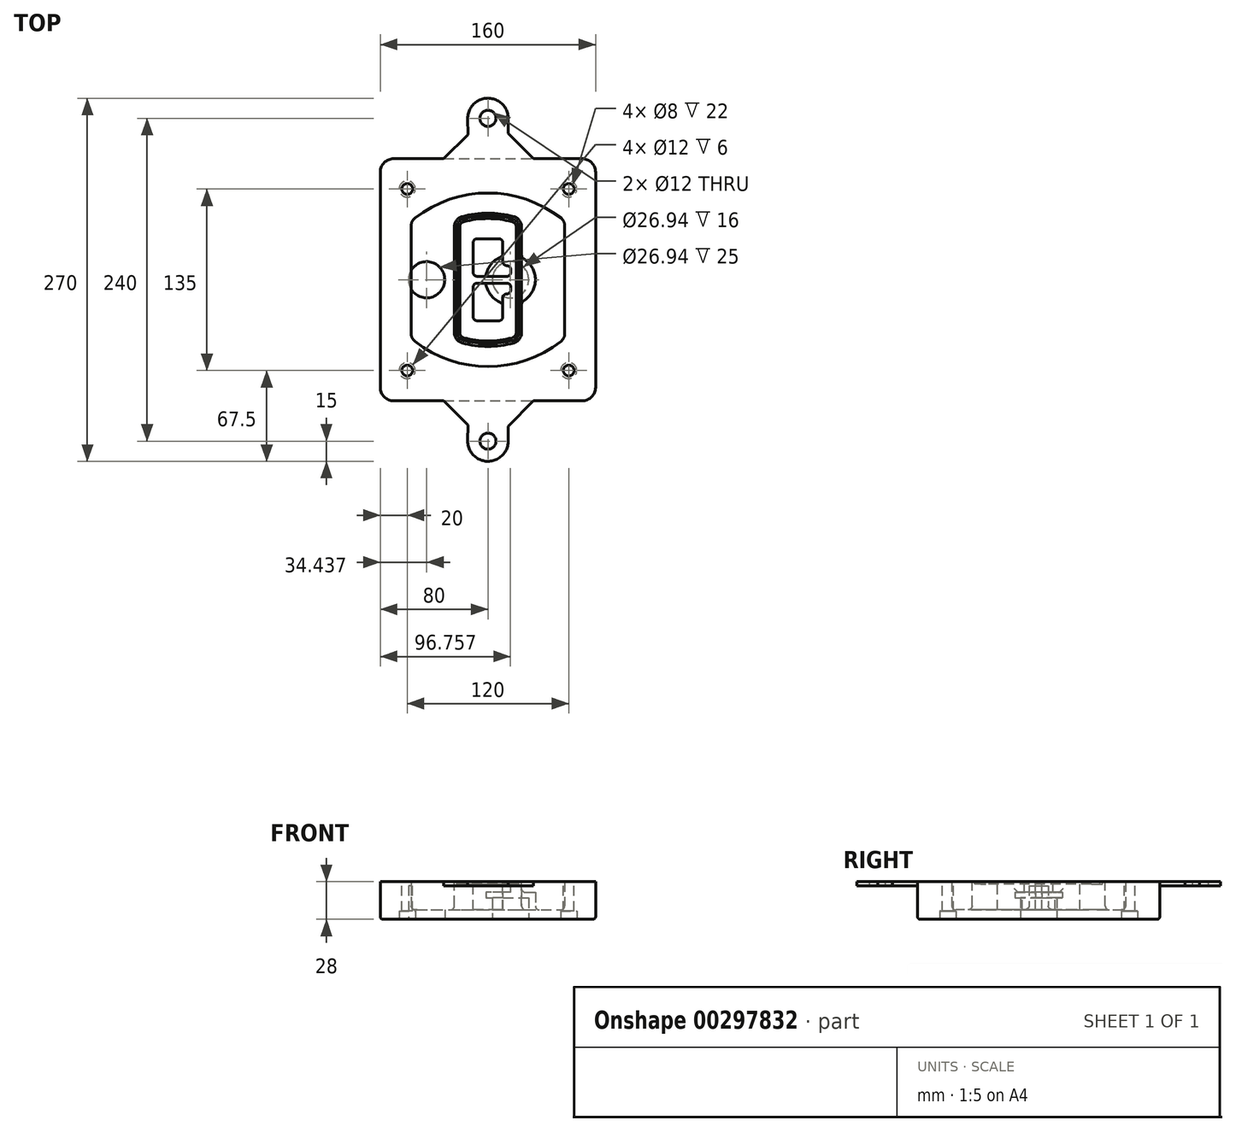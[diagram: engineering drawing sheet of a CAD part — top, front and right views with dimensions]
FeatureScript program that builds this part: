
annotation { "Feature Type Name" : "Feature", "Feature Type Description" : "" }
export const myFeature = defineFeature(function(context is Context, id is Id, definition is map)
    precondition{}
    {
        {
            var Q0;
            Q0=qCreatedBy(makeId("Top.planeOp"),FACE);
            var sketch = newSketch(context, id + "F0", { "sketchPlane" : qUnion([Q0])});
            skPoint(sketch, "E0.rect.middle", {"position": v(0, 0) * mm});
            skLineSegment(sketch, "E1.bottom", {"start": v(-70, -90) * mm, "end": v(70, -90) * mm});
            skLineSegment(sketch, "E1.top", {"start": v(-70, 90) * mm, "end": v(70, 90) * mm});
            skLineSegment(sketch, "E1.left", {"start": v(-80, -80) * mm, "end": v(-80, 80) * mm});
            skLineSegment(sketch, "E1.right", {"start": v(80, -80) * mm, "end": v(80, 80) * mm});
            skLineSegment(sketch, "E2", {"start": v(-80, 90) * mm, "end": v(80, -90) * mm, "construction": true});
            skLineSegment(sketch, "E3", {"start": v(80, 90) * mm, "end": v(-80, -90) * mm, "construction": true});
            skCircle(sketch, "E4", {"center": v(-60, 67.5) * mm, "radius": 4 * mm});
            skCircle(sketch, "E5", {"center": v(60, 67.5) * mm, "radius": 4 * mm});
            skCircle(sketch, "E6", {"center": v(60, -67.5) * mm, "radius": 4 * mm});
            skCircle(sketch, "E7", {"center": v(-60, -67.5) * mm, "radius": 4 * mm});
            skLineSegment(sketch, "E8", {"start": v(-60, 67.5) * mm, "end": v(60, 67.5) * mm, "construction": true});
            skLineSegment(sketch, "E9", {"start": v(60, 67.5) * mm, "end": v(60, -67.5) * mm, "construction": true});
            skLineSegment(sketch, "E10", {"start": v(60, -67.5) * mm, "end": v(-60, -67.5) * mm, "construction": true});
            skLineSegment(sketch, "E11", {"start": v(-60, -67.5) * mm, "end": v(-60, 67.5) * mm, "construction": true});
            skLineSegment(sketch, "E12", {"start": v(-60, 40.3) * mm, "end": v(-60, -40.3) * mm});
            skLineSegment(sketch, "E13", {"start": v(60, 40.3) * mm, "end": v(60, -40.3) * mm});
            skArc(sketch, "E14", {"start": v(56.15, 48.18) * mm, "mid": v(0, 67.5) * mm, "end": v(-56.15, 48.18) * mm});
            skArc(sketch, "E15", {"start": v(-56.15, -48.18) * mm, "mid": v(0, -67.5) * mm, "end": v(56.15, -48.18) * mm});
            skLineSegment(sketch, "E16", {"start": v(-60, 0) * mm, "end": v(60, 0) * mm, "construction": true});
            skPoint(sketch, "E17.visualSharp", {"position": v(-60, -45) * mm});
            skArc(sketch, "E17.filletArc", {"start": v(-60, -40.3) * mm, "mid": v(-58.99, -44.68) * mm, "end": v(-56.15, -48.18) * mm});
            skPoint(sketch, "E18.visualSharp", {"position": v(-60, 45) * mm});
            skArc(sketch, "E18.filletArc", {"start": v(-56.15, 48.18) * mm, "mid": v(-58.99, 44.68) * mm, "end": v(-60, 40.3) * mm});
            skPoint(sketch, "E19.visualSharp", {"position": v(60, 45) * mm});
            skArc(sketch, "E19.filletArc", {"start": v(60, 40.3) * mm, "mid": v(58.99, 44.68) * mm, "end": v(56.15, 48.18) * mm});
            skPoint(sketch, "E20.visualSharp", {"position": v(60, -45) * mm});
            skArc(sketch, "E20.filletArc", {"start": v(56.15, -48.18) * mm, "mid": v(58.99, -44.68) * mm, "end": v(60, -40.3) * mm});
            skPoint(sketch, "E21.visualSharp", {"position": v(-80, 90) * mm});
            skArc(sketch, "E21.filletArc", {"start": v(-70, 90) * mm, "mid": v(-77.07, 87.07) * mm, "end": v(-80, 80) * mm});
            skPoint(sketch, "E22.visualSharp", {"position": v(80, 90) * mm});
            skArc(sketch, "E22.filletArc", {"start": v(80, 80) * mm, "mid": v(77.07, 87.07) * mm, "end": v(70, 90) * mm});
            skPoint(sketch, "E23.visualSharp", {"position": v(80, -90) * mm});
            skArc(sketch, "E23.filletArc", {"start": v(70, -90) * mm, "mid": v(77.07, -87.07) * mm, "end": v(80, -80) * mm});
            skPoint(sketch, "E24.visualSharp", {"position": v(-80, -90) * mm});
            skArc(sketch, "E24.filletArc", {"start": v(-80, -80) * mm, "mid": v(-77.07, -87.07) * mm, "end": v(-70, -90) * mm});
            skArc(sketch, "E25.0", {"start": v(57, 40.3) * mm, "mid": v(56.3, 43.36) * mm, "end": v(54.3, 45.81) * mm});
            skLineSegment(sketch, "E25.1", {"start": v(57, 40.3) * mm, "end": v(57, -40.3) * mm});
            skArc(sketch, "E25.2", {"start": v(54.3, -45.81) * mm, "mid": v(56.3, -43.36) * mm, "end": v(57, -40.3) * mm});
            skArc(sketch, "E25.3", {"start": v(-54.3, -45.81) * mm, "mid": v(0, -64.5) * mm, "end": v(54.3, -45.81) * mm});
            skArc(sketch, "E25.4", {"start": v(-57, -40.3) * mm, "mid": v(-56.3, -43.36) * mm, "end": v(-54.3, -45.81) * mm});
            skArc(sketch, "E25.5", {"start": v(54.3, 45.81) * mm, "mid": v(0, 64.5) * mm, "end": v(-54.3, 45.81) * mm});
            skLineSegment(sketch, "E25.6", {"start": v(-57, 40.3) * mm, "end": v(-57, -40.3) * mm});
            skArc(sketch, "E25.7", {"start": v(-54.3, 45.81) * mm, "mid": v(-56.3, 43.36) * mm, "end": v(-57, 40.3) * mm});
            skArc(sketch, "E26.0", {"start": v(-58.62, 51.33) * mm, "mid": v(-62.58, 46.43) * mm, "end": v(-64, 40.3) * mm});
            skArc(sketch, "E26.1", {"start": v(58.62, 51.33) * mm, "mid": v(0, 71.5) * mm, "end": v(-58.62, 51.33) * mm});
            skArc(sketch, "E26.2", {"start": v(64, 40.3) * mm, "mid": v(62.58, 46.43) * mm, "end": v(58.62, 51.33) * mm});
            skLineSegment(sketch, "E26.3", {"start": v(64, 40.3) * mm, "end": v(64, -40.3) * mm});
            skArc(sketch, "E26.4", {"start": v(58.62, -51.33) * mm, "mid": v(62.58, -46.43) * mm, "end": v(64, -40.3) * mm});
            skLineSegment(sketch, "E26.5", {"start": v(-64, 40.3) * mm, "end": v(-64, -40.3) * mm});
            skArc(sketch, "E26.6", {"start": v(-58.62, -51.33) * mm, "mid": v(0, -71.5) * mm, "end": v(58.62, -51.33) * mm});
            skArc(sketch, "E26.7", {"start": v(-64, -40.3) * mm, "mid": v(-62.58, -46.43) * mm, "end": v(-58.62, -51.33) * mm});
            skSolve(sketch);
        }
        {
            var Q0;
            Q0=makeQuery(id+"F0.imprint","IMPRINT",FACE,{"disambiguationData":[TD([[makeQuery(id+"F0.imprint","IMPRINT",EDGE,{"derivedFrom":sQuery(id+"F0.wireOp",EDGE,"E1.bottom")}),1.0]])]});
            var Q1;
            Q1=makeQuery(id+"F0.imprint","IMPRINT",FACE,{"disambiguationData":[TD([[makeQuery(id+"F0.imprint","IMPRINT",EDGE,{"derivedFrom":sQuery(id+"F0.wireOp",EDGE,"E12")}),1.0]])]});
            var Q2;
            Q2=makeQuery(id+"F0.imprint","IMPRINT",FACE,{"disambiguationData":[TD([[makeQuery(id+"F0.imprint","IMPRINT",EDGE,{"derivedFrom":sQuery(id+"F0.wireOp",EDGE,"E25.0")}),1.0]])]});
            var Q3;
            Q3=makeQuery(id+"F0.imprint","IMPRINT",FACE,{"disambiguationData":[TD([[makeQuery(id+"F0.imprint","IMPRINT",EDGE,{"derivedFrom":sQuery(id+"F0.wireOp",EDGE,"E12")}),-1.0]])]});
            extrude(context, id + "F1", {"entities" : qUnion([Q0, Q1, Q2, Q3]), "oppositeDirection" : true, "depth" : 25 * mm});
        }
        {
            var Q0;
            Q0=makeQuery(id+"F0.imprint","IMPRINT",FACE,{"disambiguationData":[TD([[makeQuery(id+"F0.imprint","IMPRINT",EDGE,{"derivedFrom":sQuery(id+"F0.wireOp",EDGE,"E12")}),1.0]])]});
            extrude(context, id + "F2", {"entities" : qUnion([Q0]), "operationType" : NewBodyOperationType.ADD, "depth" : 3 * mm});
        }
        {
            var Q0;
            Q0=makeQuery(id+"F0.imprint","IMPRINT",FACE,{"disambiguationData":[TD([[makeQuery(id+"F0.imprint","IMPRINT",EDGE,{"derivedFrom":sQuery(id+"F0.wireOp",EDGE,"E25.0")}),1.0]])]});
            extrude(context, id + "F3", {"entities" : qUnion([Q0]), "operationType" : NewBodyOperationType.REMOVE, "oppositeDirection" : true, "depth" : 18 * mm});
        }
        {
            var Q0;
            Q0=makeQuery(id+"F2.opExtrude","CAP_FACE",FACE,{"disambiguationData":[OSD([sQuery(id+"F0.wireOp",EDGE,"E12"),sQuery(id+"F0.wireOp",EDGE,"E13"),sQuery(id+"F0.wireOp",EDGE,"E14"),sQuery(id+"F0.wireOp",EDGE,"E15"),sQuery(id+"F0.wireOp",EDGE,"E17.filletArc"),sQuery(id+"F0.wireOp",EDGE,"E18.filletArc"),sQuery(id+"F0.wireOp",EDGE,"E19.filletArc"),sQuery(id+"F0.wireOp",EDGE,"E20.filletArc"),sQuery(id+"F0.wireOp",EDGE,"E25.0"),sQuery(id+"F0.wireOp",EDGE,"E25.1"),sQuery(id+"F0.wireOp",EDGE,"E25.2"),sQuery(id+"F0.wireOp",EDGE,"E25.3"),sQuery(id+"F0.wireOp",EDGE,"E25.4"),sQuery(id+"F0.wireOp",EDGE,"E25.5"),sQuery(id+"F0.wireOp",EDGE,"E25.6"),sQuery(id+"F0.wireOp",EDGE,"E25.7")])],"isStart":false});
            var sketch = newSketch(context, id + "F4", { "sketchPlane" : qUnion([Q0])});
            skArc(sketch, "E27.0", {"start": v(-19.08, -46.97) * mm, "mid": v(0, -49.5) * mm, "end": v(19.08, -46.97) * mm});
            skArc(sketch, "E28.0", {"start": v(19.08, 46.97) * mm, "mid": v(0, 49.5) * mm, "end": v(-19.08, 46.97) * mm});
            skLineSegment(sketch, "E29", {"start": v(-25, 39.25) * mm, "end": v(-25, -39.25) * mm});
            skLineSegment(sketch, "E30", {"start": v(25, 39.25) * mm, "end": v(25, -39.25) * mm});
            skLineSegment(sketch, "E31", {"start": v(-25, 45.1) * mm, "end": v(25, 45.1) * mm, "construction": true});
            skLineSegment(sketch, "E32", {"start": v(-25, -45.1) * mm, "end": v(25, -45.1) * mm, "construction": true});
            skPoint(sketch, "E33.visualSharp", {"position": v(-25, 45.1) * mm});
            skArc(sketch, "E33.filletArc", {"start": v(-19.08, 46.97) * mm, "mid": v(-23.35, 44.11) * mm, "end": v(-25, 39.25) * mm});
            skPoint(sketch, "E34.visualSharp", {"position": v(25, 45.1) * mm});
            skArc(sketch, "E34.filletArc", {"start": v(25, 39.25) * mm, "mid": v(23.35, 44.11) * mm, "end": v(19.08, 46.97) * mm});
            skPoint(sketch, "E35.visualSharp", {"position": v(25, -45.1) * mm});
            skArc(sketch, "E35.filletArc", {"start": v(19.08, -46.97) * mm, "mid": v(23.35, -44.11) * mm, "end": v(25, -39.25) * mm});
            skPoint(sketch, "E36.visualSharp", {"position": v(-25, -45.1) * mm});
            skArc(sketch, "E36.filletArc", {"start": v(-25, -39.25) * mm, "mid": v(-23.35, -44.11) * mm, "end": v(-19.08, -46.97) * mm});
            skArc(sketch, "E37.0", {"start": v(54.3, 45.81) * mm, "mid": v(0, 64.5) * mm, "end": v(-54.3, 45.81) * mm});
            skArc(sketch, "E37.1", {"start": v(-54.3, 45.81) * mm, "mid": v(-56.3, 43.36) * mm, "end": v(-57, 40.3) * mm});
            skLineSegment(sketch, "E37.2", {"start": v(-57, 40.3) * mm, "end": v(-57, -40.3) * mm});
            skArc(sketch, "E37.3", {"start": v(-57, -40.3) * mm, "mid": v(-56.3, -43.36) * mm, "end": v(-54.3, -45.81) * mm});
            skArc(sketch, "E37.4", {"start": v(-54.3, -45.81) * mm, "mid": v(0, -64.5) * mm, "end": v(54.3, -45.81) * mm});
            skArc(sketch, "E37.5", {"start": v(54.3, -45.81) * mm, "mid": v(56.3, -43.36) * mm, "end": v(57, -40.3) * mm});
            skLineSegment(sketch, "E37.6", {"start": v(57, 40.3) * mm, "end": v(57, -40.3) * mm});
            skArc(sketch, "E37.7", {"start": v(57, 40.3) * mm, "mid": v(56.3, 43.36) * mm, "end": v(54.3, 45.81) * mm});
            skLineSegment(sketch, "E38.0", {"start": v(23, 39.25) * mm, "end": v(23, -39.25) * mm});
            skArc(sketch, "E38.1", {"start": v(18.56, -45.04) * mm, "mid": v(21.76, -42.9) * mm, "end": v(23, -39.25) * mm});
            skArc(sketch, "E38.2", {"start": v(-18.56, -45.04) * mm, "mid": v(0, -47.5) * mm, "end": v(18.56, -45.04) * mm});
            skArc(sketch, "E38.3", {"start": v(-23, -39.25) * mm, "mid": v(-21.76, -42.9) * mm, "end": v(-18.56, -45.04) * mm});
            skLineSegment(sketch, "E38.4", {"start": v(-23, 39.25) * mm, "end": v(-23, -39.25) * mm});
            skArc(sketch, "E38.5", {"start": v(23, 39.25) * mm, "mid": v(21.76, 42.9) * mm, "end": v(18.56, 45.04) * mm});
            skArc(sketch, "E38.6", {"start": v(-18.56, 45.04) * mm, "mid": v(-21.76, 42.9) * mm, "end": v(-23, 39.25) * mm});
            skArc(sketch, "E38.7", {"start": v(18.56, 45.04) * mm, "mid": v(0, 47.5) * mm, "end": v(-18.56, 45.04) * mm});
            skArc(sketch, "E39.0", {"start": v(21, 39.25) * mm, "mid": v(20.18, 41.68) * mm, "end": v(18.04, 43.1) * mm});
            skLineSegment(sketch, "E39.1", {"start": v(21, 39.25) * mm, "end": v(21, -39.25) * mm});
            skArc(sketch, "E39.2", {"start": v(18.04, -43.1) * mm, "mid": v(20.18, -41.68) * mm, "end": v(21, -39.25) * mm});
            skArc(sketch, "E39.3", {"start": v(-18.04, -43.1) * mm, "mid": v(0, -45.5) * mm, "end": v(18.04, -43.1) * mm});
            skArc(sketch, "E39.4", {"start": v(-21, -39.25) * mm, "mid": v(-20.18, -41.68) * mm, "end": v(-18.04, -43.1) * mm});
            skArc(sketch, "E39.5", {"start": v(18.04, 43.1) * mm, "mid": v(0, 45.5) * mm, "end": v(-18.04, 43.1) * mm});
            skLineSegment(sketch, "E39.6", {"start": v(-21, 39.25) * mm, "end": v(-21, -39.25) * mm});
            skArc(sketch, "E39.7", {"start": v(-18.04, 43.1) * mm, "mid": v(-20.18, 41.68) * mm, "end": v(-21, 39.25) * mm});
            skLineSegment(sketch, "E40", {"start": v(-25, 0) * mm, "end": v(25, 0) * mm, "construction": true});
            skLineSegment(sketch, "E41", {"start": v(-11, 5.5) * mm, "end": v(-11, 27.5) * mm});
            skLineSegment(sketch, "E42", {"start": v(-8, 30.5) * mm, "end": v(8, 30.5) * mm});
            skLineSegment(sketch, "E43", {"start": v(11, 27.5) * mm, "end": v(11, 13.5) * mm});
            skLineSegment(sketch, "E44", {"start": v(14, 10.5) * mm, "end": v(14, 10.5) * mm});
            skLineSegment(sketch, "E45", {"start": v(17, 7.5) * mm, "end": v(17, 5.5) * mm});
            skLineSegment(sketch, "E46", {"start": v(14, 2.5) * mm, "end": v(-8, 2.5) * mm});
            skPoint(sketch, "E47.visualSharp", {"position": v(-11, 30.5) * mm});
            skArc(sketch, "E47.filletArc", {"start": v(-8, 30.5) * mm, "mid": v(-10.12, 29.62) * mm, "end": v(-11, 27.5) * mm});
            skPoint(sketch, "E48.visualSharp", {"position": v(11, 30.5) * mm});
            skArc(sketch, "E48.filletArc", {"start": v(11, 27.5) * mm, "mid": v(10.12, 29.62) * mm, "end": v(8, 30.5) * mm});
            skPoint(sketch, "E49.visualSharp", {"position": v(11, 10.5) * mm});
            skArc(sketch, "E49.filletArc", {"start": v(11, 13.5) * mm, "mid": v(11.88, 11.38) * mm, "end": v(14, 10.5) * mm});
            skPoint(sketch, "E50.visualSharp", {"position": v(17, 10.5) * mm});
            skArc(sketch, "E50.filletArc", {"start": v(17, 7.5) * mm, "mid": v(16.12, 9.62) * mm, "end": v(14, 10.5) * mm});
            skPoint(sketch, "E51.visualSharp", {"position": v(17, 2.5) * mm});
            skArc(sketch, "E51.filletArc", {"start": v(14, 2.5) * mm, "mid": v(16.12, 3.38) * mm, "end": v(17, 5.5) * mm});
            skPoint(sketch, "E52.visualSharp", {"position": v(-11, 2.5) * mm});
            skArc(sketch, "E52.filletArc", {"start": v(-11, 5.5) * mm, "mid": v(-10.12, 3.38) * mm, "end": v(-8, 2.5) * mm});
            skLineSegment(sketch, "E53.0.MirrorCS", {"start": v(14, -2.5) * mm, "end": v(-8, -2.5) * mm});
            skArc(sketch, "E54.0.MirrorCS", {"start": v(-11, -5.5) * mm, "mid": v(-10.12, -3.38) * mm, "end": v(-8, -2.5) * mm});
            skLineSegment(sketch, "E55.0.MirrorCS", {"start": v(-11, -5.5) * mm, "end": v(-11, -27.5) * mm});
            skArc(sketch, "E56.0.MirrorCS", {"start": v(-8, -30.5) * mm, "mid": v(-10.12, -29.62) * mm, "end": v(-11, -27.5) * mm});
            skLineSegment(sketch, "E57.0.MirrorCS", {"start": v(-8, -30.5) * mm, "end": v(8, -30.5) * mm});
            skArc(sketch, "E58.0.MirrorCS", {"start": v(11, -27.5) * mm, "mid": v(10.12, -29.62) * mm, "end": v(8, -30.5) * mm});
            skLineSegment(sketch, "E59.0.MirrorCS", {"start": v(11, -27.5) * mm, "end": v(11, -13.5) * mm});
            skArc(sketch, "E60.0.MirrorCS", {"start": v(11, -13.5) * mm, "mid": v(11.88, -11.38) * mm, "end": v(14, -10.5) * mm});
            skArc(sketch, "E61.0.MirrorCS", {"start": v(17, -7.5) * mm, "mid": v(16.12, -9.62) * mm, "end": v(14, -10.5) * mm});
            skLineSegment(sketch, "E62.0.MirrorCS", {"start": v(17, -7.5) * mm, "end": v(17, -5.5) * mm});
            skArc(sketch, "E63.0.MirrorCS", {"start": v(14, -2.5) * mm, "mid": v(16.12, -3.38) * mm, "end": v(17, -5.5) * mm});
            skSolve(sketch);
        }
        {
            var Q0;
            Q0=makeQuery(id+"F4.imprint","IMPRINT",FACE,{"disambiguationData":[TD([[makeQuery(id+"F4.imprint","IMPRINT",EDGE,{"derivedFrom":sQuery(id+"F4.wireOp",EDGE,"E27.0")}),1.0]])]});
            var Q1;
            Q1=makeQuery(id+"F4.imprint","IMPRINT",FACE,{"disambiguationData":[TD([[makeQuery(id+"F4.imprint","IMPRINT",EDGE,{"derivedFrom":sQuery(id+"F4.wireOp",EDGE,"E38.0")}),-1.0]])]});
            var Q2;
            Q2=makeQuery(id+"F4.imprint","IMPRINT",FACE,{"disambiguationData":[TD([[makeQuery(id+"F4.imprint","IMPRINT",EDGE,{"derivedFrom":sQuery(id+"F4.wireOp",EDGE,"E39.0")}),1.0]])]});
            extrude(context, id + "F5", {"entities" : qUnion([Q0, Q1, Q2]), "operationType" : NewBodyOperationType.ADD, "endBound" : BoundingType.UP_TO_NEXT, "oppositeDirection" : true, "depth" : 25 * mm});
        }
        {
            var Q0;
            Q0=makeQuery(id+"F4.imprint","IMPRINT",FACE,{"disambiguationData":[TD([[makeQuery(id+"F4.imprint","IMPRINT",EDGE,{"derivedFrom":sQuery(id+"F4.wireOp",EDGE,"E38.0")}),-1.0]])]});
            extrude(context, id + "F6", {"entities" : qUnion([Q0]), "operationType" : NewBodyOperationType.REMOVE, "oppositeDirection" : true, "depth" : 2 * mm});
        }
        {
            var Q0;
            Q0=makeQuery(id+"F1.opExtrude","CAP_FACE",FACE,{"disambiguationData":[OSD([sQuery(id+"F0.wireOp",EDGE,"E1.bottom"),sQuery(id+"F0.wireOp",EDGE,"E1.top"),sQuery(id+"F0.wireOp",EDGE,"E1.left"),sQuery(id+"F0.wireOp",EDGE,"E1.right"),sQuery(id+"F0.wireOp",EDGE,"E4"),sQuery(id+"F0.wireOp",EDGE,"E5"),sQuery(id+"F0.wireOp",EDGE,"E6"),sQuery(id+"F0.wireOp",EDGE,"E7"),sQuery(id+"F0.wireOp",EDGE,"E21.filletArc"),sQuery(id+"F0.wireOp",EDGE,"E22.filletArc"),sQuery(id+"F0.wireOp",EDGE,"E23.filletArc"),sQuery(id+"F0.wireOp",EDGE,"E24.filletArc")])],"isStart":false});
            var sketch = newSketch(context, id + "F7", { "sketchPlane" : qUnion([Q0])});
            skCircle(sketch, "E64", {"center": v(16.76, 0) * mm, "radius": 13.47 * mm});
            skCircle(sketch, "E65", {"center": v(-45.56, 0) * mm, "radius": 13.47 * mm});
            skLineSegment(sketch, "E66", {"start": v(80, 0) * mm, "end": v(-80, 0) * mm});
            skCircle(sketch, "E67", {"center": v(16.76, 0) * mm, "radius": 18.47 * mm});
            skCircle(sketch, "E68", {"center": v(60, -67.5) * mm, "radius": 6 * mm});
            skCircle(sketch, "E69", {"center": v(-60, -67.5) * mm, "radius": 6 * mm});
            skCircle(sketch, "E70", {"center": v(-60, 67.5) * mm, "radius": 6 * mm});
            skCircle(sketch, "E71", {"center": v(60, 67.5) * mm, "radius": 6 * mm});
            skSolve(sketch);
        }
        {
            var Q0;
            {var subQ1=sQuery(id+"F7.wireOp",EDGE,"E66");var subQ4=sQuery(id+"F7.wireOp",EDGE,"E64");var subQ6=makeQuery(id+"F7.imprint","INTERSECT",VERTEX,{"disambiguationData":[OD(0.0)],"derivedFrom":[subQ4,subQ1]});Q0=makeQuery(id+"F7.imprint","IMPRINT",FACE,{"disambiguationData":[TD([[makeQuery(id+"F7.imprint","IMPRINT",EDGE,{"disambiguationData":[TD([[subQ6,-1.0]])],"derivedFrom":subQ4}),-1.0]])]});}
            var Q1;
            {var subQ0=sQuery(id+"F7.wireOp",EDGE,"E66");var subQ1=sQuery(id+"F7.wireOp",EDGE,"E64");var subQ3=makeQuery(id+"F7.imprint","INTERSECT",VERTEX,{"disambiguationData":[OD(0.0)],"derivedFrom":[subQ1,subQ0]});Q1=makeQuery(id+"F7.imprint","IMPRINT",FACE,{"disambiguationData":[TD([[makeQuery(id+"F7.imprint","IMPRINT",EDGE,{"disambiguationData":[TD([[subQ3,-1.0]])],"derivedFrom":subQ1}),1.0]])]});}
            var Q2;
            {var subQ0=sQuery(id+"F7.wireOp",EDGE,"E66");var subQ1=sQuery(id+"F7.wireOp",EDGE,"E64");var subQ3=makeQuery(id+"F7.imprint","INTERSECT",VERTEX,{"disambiguationData":[OD(0.0)],"derivedFrom":[subQ1,subQ0]});Q2=makeQuery(id+"F7.imprint","IMPRINT",FACE,{"disambiguationData":[TD([[makeQuery(id+"F7.imprint","IMPRINT",EDGE,{"disambiguationData":[TD([[subQ3,1.0]])],"derivedFrom":subQ1}),1.0]])]});}
            var Q3;
            {var subQ1=sQuery(id+"F7.wireOp",EDGE,"E66");var subQ4=sQuery(id+"F7.wireOp",EDGE,"E64");var subQ6=makeQuery(id+"F7.imprint","INTERSECT",VERTEX,{"disambiguationData":[OD(0.0)],"derivedFrom":[subQ4,subQ1]});Q3=makeQuery(id+"F7.imprint","IMPRINT",FACE,{"disambiguationData":[TD([[makeQuery(id+"F7.imprint","IMPRINT",EDGE,{"disambiguationData":[TD([[subQ6,1.0]])],"derivedFrom":subQ4}),-1.0]])]});}
            extrude(context, id + "F8", {"entities" : qUnion([Q0, Q1, Q2, Q3]), "operationType" : NewBodyOperationType.ADD, "oppositeDirection" : true, "depth" : 20 * mm});
        }
        {
            var Q0;
            {var subQ0=sQuery(id+"F7.wireOp",EDGE,"E66");var subQ1=sQuery(id+"F7.wireOp",EDGE,"E64");var subQ3=makeQuery(id+"F7.imprint","INTERSECT",VERTEX,{"disambiguationData":[OD(0.0)],"derivedFrom":[subQ1,subQ0]});Q0=makeQuery(id+"F7.imprint","IMPRINT",FACE,{"disambiguationData":[TD([[makeQuery(id+"F7.imprint","IMPRINT",EDGE,{"disambiguationData":[TD([[subQ3,-1.0]])],"derivedFrom":subQ1}),1.0]])]});}
            var Q1;
            {var subQ0=sQuery(id+"F7.wireOp",EDGE,"E66");var subQ1=sQuery(id+"F7.wireOp",EDGE,"E64");var subQ3=makeQuery(id+"F7.imprint","INTERSECT",VERTEX,{"disambiguationData":[OD(0.0)],"derivedFrom":[subQ1,subQ0]});Q1=makeQuery(id+"F7.imprint","IMPRINT",FACE,{"disambiguationData":[TD([[makeQuery(id+"F7.imprint","IMPRINT",EDGE,{"disambiguationData":[TD([[subQ3,1.0]])],"derivedFrom":subQ1}),1.0]])]});}
            extrude(context, id + "F9", {"entities" : qUnion([Q0, Q1]), "operationType" : NewBodyOperationType.REMOVE, "oppositeDirection" : true, "depth" : 16 * mm});
        }
        {
            var Q0;
            {var subQ0=sQuery(id+"F7.wireOp",EDGE,"E66");var subQ1=sQuery(id+"F7.wireOp",EDGE,"E65");var subQ3=makeQuery(id+"F7.imprint","INTERSECT",VERTEX,{"disambiguationData":[OD(0.0)],"derivedFrom":[subQ1,subQ0]});Q0=makeQuery(id+"F7.imprint","IMPRINT",FACE,{"disambiguationData":[TD([[makeQuery(id+"F7.imprint","IMPRINT",EDGE,{"disambiguationData":[TD([[subQ3,-1.0]])],"derivedFrom":subQ1}),1.0]])]});}
            var Q1;
            {var subQ0=sQuery(id+"F7.wireOp",EDGE,"E66");var subQ1=sQuery(id+"F7.wireOp",EDGE,"E65");var subQ3=makeQuery(id+"F7.imprint","INTERSECT",VERTEX,{"disambiguationData":[OD(0.0)],"derivedFrom":[subQ1,subQ0]});Q1=makeQuery(id+"F7.imprint","IMPRINT",FACE,{"disambiguationData":[TD([[makeQuery(id+"F7.imprint","IMPRINT",EDGE,{"disambiguationData":[TD([[subQ3,1.0]])],"derivedFrom":subQ1}),1.0]])]});}
            extrude(context, id + "F10", {"entities" : qUnion([Q0, Q1]), "operationType" : NewBodyOperationType.REMOVE, "oppositeDirection" : true, "depth" : 25 * mm});
        }
        {
            var Q0;
            Q0=makeQuery(id+"F7.imprint","IMPRINT",FACE,{"disambiguationData":[TD([[makeQuery(id+"F7.imprint","IMPRINT",EDGE,{"derivedFrom":sQuery(id+"F7.wireOp",EDGE,"E68")}),1.0]])]});
            var Q1;
            Q1=makeQuery(id+"F7.imprint","IMPRINT",FACE,{"disambiguationData":[TD([[makeQuery(id+"F7.imprint","IMPRINT",EDGE,{"derivedFrom":makeQuery(id+"F1.opExtrude","CAP_EDGE",EDGE,{"disambiguationData":[OSD([sQuery(id+"F0.wireOp",EDGE,"E5")])],"isStart":false})}),-1.0]])]});
            var Q2;
            Q2=makeQuery(id+"F7.imprint","IMPRINT",FACE,{"disambiguationData":[TD([[makeQuery(id+"F7.imprint","IMPRINT",EDGE,{"derivedFrom":sQuery(id+"F7.wireOp",EDGE,"E69")}),1.0]])]});
            var Q3;
            Q3=makeQuery(id+"F7.imprint","IMPRINT",FACE,{"disambiguationData":[TD([[makeQuery(id+"F7.imprint","IMPRINT",EDGE,{"derivedFrom":makeQuery(id+"F1.opExtrude","CAP_EDGE",EDGE,{"disambiguationData":[OSD([sQuery(id+"F0.wireOp",EDGE,"E4")])],"isStart":false})}),-1.0]])]});
            var Q4;
            Q4=makeQuery(id+"F7.imprint","IMPRINT",FACE,{"disambiguationData":[TD([[makeQuery(id+"F7.imprint","IMPRINT",EDGE,{"derivedFrom":sQuery(id+"F7.wireOp",EDGE,"E70")}),1.0]])]});
            var Q5;
            Q5=makeQuery(id+"F7.imprint","IMPRINT",FACE,{"disambiguationData":[TD([[makeQuery(id+"F7.imprint","IMPRINT",EDGE,{"derivedFrom":makeQuery(id+"F1.opExtrude","CAP_EDGE",EDGE,{"disambiguationData":[OSD([sQuery(id+"F0.wireOp",EDGE,"E7")])],"isStart":false})}),-1.0]])]});
            var Q6;
            Q6=makeQuery(id+"F7.imprint","IMPRINT",FACE,{"disambiguationData":[TD([[makeQuery(id+"F7.imprint","IMPRINT",EDGE,{"derivedFrom":sQuery(id+"F7.wireOp",EDGE,"E71")}),1.0]])]});
            var Q7;
            Q7=makeQuery(id+"F7.imprint","IMPRINT",FACE,{"disambiguationData":[TD([[makeQuery(id+"F7.imprint","IMPRINT",EDGE,{"derivedFrom":makeQuery(id+"F1.opExtrude","CAP_EDGE",EDGE,{"disambiguationData":[OSD([sQuery(id+"F0.wireOp",EDGE,"E6")])],"isStart":false})}),-1.0]])]});
            extrude(context, id + "F11", {"entities" : qUnion([Q0, Q1, Q2, Q3, Q4, Q5, Q6, Q7]), "operationType" : NewBodyOperationType.REMOVE, "oppositeDirection" : true, "depth" : 6 * mm});
        }
        {
            var Q0;
            Q0=makeQuery(id+"F9.boolean.opBoolean","COPY",FACE,{"derivedFrom":makeQuery(id+"F9.opExtrude","CAP_FACE",FACE,{"disambiguationData":[OSD([sQuery(id+"F7.wireOp",EDGE,"E64")])],"isStart":false})});
            var sketch = newSketch(context, id + "F12", { "sketchPlane" : qUnion([Q0])});
            skArc(sketch, "E72.0", {"start": v(11, 17.55) * mm, "mid": v(2.57, 11.82) * mm, "end": v(-1.54, 2.5) * mm});
            skArc(sketch, "E72.1", {"start": v(-1.54, -2.5) * mm, "mid": v(2.57, -11.82) * mm, "end": v(11, -17.55) * mm});
            skLineSegment(sketch, "E73", {"start": v(-1.54, -2.5) * mm, "end": v(14, -2.5) * mm});
            skLineSegment(sketch, "E74.0", {"start": v(14, 2.5) * mm, "end": v(-1.54, 2.5) * mm});
            skArc(sketch, "E74.1", {"start": v(14, 2.5) * mm, "mid": v(16.12, 3.38) * mm, "end": v(17, 5.5) * mm});
            skLineSegment(sketch, "E74.2", {"start": v(17, 7.5) * mm, "end": v(17, 5.5) * mm});
            skArc(sketch, "E74.3", {"start": v(17, 7.5) * mm, "mid": v(16.12, 9.62) * mm, "end": v(14, 10.5) * mm});
            skArc(sketch, "E74.4", {"start": v(11, 13.5) * mm, "mid": v(11.88, 11.38) * mm, "end": v(14, 10.5) * mm});
            skLineSegment(sketch, "E74.5", {"start": v(11, 17.55) * mm, "end": v(11, 13.5) * mm});
            skLineSegment(sketch, "E74.7", {"start": v(14, -2.5) * mm, "end": v(-1.54, -2.5) * mm});
            skArc(sketch, "E74.8", {"start": v(14, -2.5) * mm, "mid": v(16.12, -3.38) * mm, "end": v(17, -5.5) * mm});
            skLineSegment(sketch, "E74.9", {"start": v(17, -7.5) * mm, "end": v(17, -5.5) * mm});
            skArc(sketch, "E74.10", {"start": v(17, -7.5) * mm, "mid": v(16.12, -9.62) * mm, "end": v(14, -10.5) * mm});
            skArc(sketch, "E74.11", {"start": v(11, -13.5) * mm, "mid": v(11.88, -11.38) * mm, "end": v(14, -10.5) * mm});
            skLineSegment(sketch, "E74.12", {"start": v(11, -17.55) * mm, "end": v(11, -13.5) * mm});
            skPoint(sketch, "E75.orphan", {"position": v(11, -27.5) * mm});
            skPoint(sketch, "E76.orphan", {"position": v(-8, -2.5) * mm});
            skPoint(sketch, "E77.orphan", {"position": v(-8, 2.5) * mm});
            skPoint(sketch, "E78.orphan", {"position": v(11, 27.5) * mm});
            skSolve(sketch);
        }
        {
            var Q0;
            {var subQ7=sQuery(id+"F12.wireOp",EDGE,"E72.0");var subQ14=sQuery(id+"F12.wireOp",EDGE,"E72.1");var subQ16=sQuery(id+"F12.wireOp",EDGE,"E74.1");var subQ18=sQuery(id+"F12.wireOp",EDGE,"E74.8");Q0=qUnion([makeQuery(id+"F12.imprint","IMPRINT",FACE,{"disambiguationData":[TD([[makeQuery(id+"F12.imprint","IMPRINT",EDGE,{"derivedFrom":subQ7}),1.0]])]}),makeQuery(id+"F12.imprint","IMPRINT",FACE,{"disambiguationData":[TD([[makeQuery(id+"F12.imprint","IMPRINT",EDGE,{"derivedFrom":subQ14}),1.0]])]}),makeQuery(id+"F12.imprint","IMPRINT",FACE,{"disambiguationData":[TD([[makeQuery(id+"F12.imprint","IMPRINT",EDGE,{"derivedFrom":subQ16}),1.0]])]}),makeQuery(id+"F12.imprint","IMPRINT",FACE,{"disambiguationData":[TD([[makeQuery(id+"F12.imprint","IMPRINT",EDGE,{"derivedFrom":subQ18}),-1.0]])]})]);}
            var Q1;
            Q1=makeQuery(id+"F5.boolean.opBoolean","SPLIT",FACE,{"disambiguationData":[TD([makeQuery(id+"F5.opExtrude","SWEPT_FACE",FACE,{"disambiguationData":[OSD([sQuery(id+"F4.wireOp",EDGE,"E41")])]})])],"derivedFrom":makeQuery(id+"F3.boolean.opBoolean","COPY",FACE,{"derivedFrom":makeQuery(id+"F3.opExtrude","CAP_FACE",FACE,{"disambiguationData":[OSD([sQuery(id+"F0.wireOp",EDGE,"E25.0"),sQuery(id+"F0.wireOp",EDGE,"E25.1"),sQuery(id+"F0.wireOp",EDGE,"E25.2"),sQuery(id+"F0.wireOp",EDGE,"E25.3"),sQuery(id+"F0.wireOp",EDGE,"E25.4"),sQuery(id+"F0.wireOp",EDGE,"E25.5"),sQuery(id+"F0.wireOp",EDGE,"E25.6"),sQuery(id+"F0.wireOp",EDGE,"E25.7")])],"isStart":false})})});
            extrude(context, id + "F13", {"entities" : qUnion([Q0]), "operationType" : NewBodyOperationType.REMOVE, "endBound" : BoundingType.UP_TO_SURFACE, "endBoundEntityFace" : qUnion([Q1]), "depth" : 25 * mm});
        }
        {
            var Q0;
            Q0=makeQuery(id+"F3.boolean.opBoolean","COPY",EDGE,{"derivedFrom":makeQuery(id+"F3.opExtrude","CAP_EDGE",EDGE,{"disambiguationData":[OSD([sQuery(id+"F0.wireOp",EDGE,"E25.6")])],"isStart":false})});
            var Q1;
            Q1=makeQuery(id+"F8.boolean.opBoolean","INTERSECT",EDGE,{"derivedFrom":[makeQuery(id+"F5.opExtrude","SWEPT_FACE",FACE,{"disambiguationData":[OSD([sQuery(id+"F4.wireOp",EDGE,"E30")])]}),makeQuery(id+"F8.opExtrude","CAP_FACE",FACE,{"disambiguationData":[OSD([sQuery(id+"F7.wireOp",EDGE,"E67")])],"isStart":false})]});
            var Q2;
            Q2=makeQuery(id+"F8.boolean.opBoolean","INTERSECT",EDGE,{"disambiguationData":[OD(1.0)],"derivedFrom":[makeQuery(id+"F5.opExtrude","SWEPT_FACE",FACE,{"disambiguationData":[OSD([sQuery(id+"F4.wireOp",EDGE,"E30")])]}),makeQuery(id+"F8.opExtrude","SWEPT_FACE",FACE,{"disambiguationData":[OSD([sQuery(id+"F7.wireOp",EDGE,"E67")])]})]});
            var Q3;
            {var subQ0=sQuery(id+"F4.wireOp",EDGE,"E30");Q3=makeQuery(id+"F8.boolean.opBoolean","SPLIT",EDGE,{"disambiguationData":[TD([makeQuery(id+"F5.opExtrude","SWEPT_FACE",FACE,{"disambiguationData":[OSD([sQuery(id+"F4.wireOp",EDGE,"E35.filletArc")])]})])],"derivedFrom":makeQuery(id+"F5.opExtrude","CAP_EDGE",EDGE,{"disambiguationData":[OSD([subQ0])],"isStart":false})});}
            var Q4;
            {var subQ0=sQuery(id+"F0.wireOp",EDGE,"E25.7");var subQ1=sQuery(id+"F0.wireOp",EDGE,"E25.1");var subQ2=sQuery(id+"F0.wireOp",EDGE,"E25.6");var subQ3=sQuery(id+"F0.wireOp",EDGE,"E25.5");var subQ4=sQuery(id+"F0.wireOp",EDGE,"E25.4");var subQ5=sQuery(id+"F0.wireOp",EDGE,"E25.0");var subQ6=sQuery(id+"F0.wireOp",EDGE,"E25.2");var subQ7=sQuery(id+"F0.wireOp",EDGE,"E25.3");Q4=makeQuery(id+"F8.boolean.opBoolean","INTERSECT",EDGE,{"derivedFrom":[makeQuery(id+"F5.boolean.opBoolean","SPLIT",FACE,{"disambiguationData":[TD([makeQuery(id+"F2.opExtrude","SWEPT_FACE",FACE,{"disambiguationData":[OSD([subQ5])]})])],"derivedFrom":makeQuery(id+"F3.boolean.opBoolean","COPY",FACE,{"derivedFrom":makeQuery(id+"F3.opExtrude","CAP_FACE",FACE,{"disambiguationData":[OSD([subQ5,subQ1,subQ6,subQ7,subQ4,subQ3,subQ2,subQ0])],"isStart":false})})}),makeQuery(id+"F8.opExtrude","SWEPT_FACE",FACE,{"disambiguationData":[OSD([sQuery(id+"F7.wireOp",EDGE,"E67")])]})]});}
            var Q5;
            Q5=makeQuery(id+"F8.boolean.opBoolean","INTERSECT",EDGE,{"disambiguationData":[OD(0.0)],"derivedFrom":[makeQuery(id+"F5.opExtrude","SWEPT_FACE",FACE,{"disambiguationData":[OSD([sQuery(id+"F4.wireOp",EDGE,"E30")])]}),makeQuery(id+"F8.opExtrude","SWEPT_FACE",FACE,{"disambiguationData":[OSD([sQuery(id+"F7.wireOp",EDGE,"E67")])]})]});
            fillet(context, id + "F14", {"entities" : qUnion([Q0, Q1, Q2, Q3, Q4, Q5]), "radius" : 3 * mm, "tangentPropagation" : true, "allowEdgeOverflow" : false});
        }
        {
            var Q0;
            Q0=makeQuery(id+"F1.opExtrude","CAP_EDGE",EDGE,{"disambiguationData":[OSD([sQuery(id+"F0.wireOp",EDGE,"E1.bottom")])],"isStart":false});
            fillet(context, id + "F15", {"entities" : qUnion([Q0]), "radius" : 2 * mm, "tangentPropagation" : true, "allowEdgeOverflow" : false});
        }
        {
            var Q0;
            {var subQ0=sQuery(id+"F0.wireOp",EDGE,"E21.filletArc");var subQ1=sQuery(id+"F0.wireOp",EDGE,"E7");var subQ2=sQuery(id+"F0.wireOp",EDGE,"E6");var subQ3=sQuery(id+"F0.wireOp",EDGE,"E5");var subQ4=sQuery(id+"F0.wireOp",EDGE,"E4");var subQ5=sQuery(id+"F0.wireOp",EDGE,"E22.filletArc");var subQ6=sQuery(id+"F0.wireOp",EDGE,"E1.bottom");var subQ7=sQuery(id+"F0.wireOp",EDGE,"E1.right");var subQ8=sQuery(id+"F0.wireOp",EDGE,"E1.top");var subQ9=sQuery(id+"F0.wireOp",EDGE,"E1.left");var subQ10=sQuery(id+"F0.wireOp",EDGE,"E23.filletArc");var subQ11=sQuery(id+"F0.wireOp",EDGE,"E24.filletArc");Q0=makeQuery(id+"F2.boolean.opBoolean","SPLIT",FACE,{"disambiguationData":[TD([makeQuery(id+"F1.opExtrude","SWEPT_FACE",FACE,{"disambiguationData":[OSD([subQ6])]})])],"derivedFrom":makeQuery(id+"F1.opExtrude","CAP_FACE",FACE,{"disambiguationData":[OSD([subQ6,subQ8,subQ9,subQ7,subQ4,subQ3,subQ2,subQ1,subQ0,subQ5,subQ10,subQ11])],"isStart":true})});}
            var sketch = newSketch(context, id + "F16", { "sketchPlane" : qUnion([Q0])});
            skLineSegment(sketch, "E79", {"start": v(0, 90) * mm, "end": v(0, 120) * mm, "construction": true});
            skCircle(sketch, "E80", {"center": v(0, 120) * mm, "radius": 6 * mm});
            skArc(sketch, "E81", {"start": v(15, 119.55) * mm, "mid": v(0.18, 135) * mm, "end": v(-15, 119.91) * mm});
            skLineSegment(sketch, "E82", {"start": v(-15, 119.91) * mm, "end": v(-14.93, 108) * mm});
            skLineSegment(sketch, "E83", {"start": v(15, 119.55) * mm, "end": v(15, 108.9) * mm});
            skLineSegment(sketch, "E84", {"start": v(-14.93, 108) * mm, "end": v(-32.93, 90) * mm});
            skLineSegment(sketch, "E85", {"start": v(15, 108.9) * mm, "end": v(33.89, 90) * mm});
            skLineSegment(sketch, "E86", {"start": v(-80, 0) * mm, "end": v(80, 0) * mm, "construction": true});
            skLineSegment(sketch, "E87.MirrorCS", {"start": v(-15, -119.91) * mm, "end": v(-14.93, -108) * mm});
            skLineSegment(sketch, "E88.MirrorCS", {"start": v(15, -119.55) * mm, "end": v(15, -108.9) * mm});
            skArc(sketch, "E89.MirrorCS", {"start": v(15, -119.55) * mm, "mid": v(0.18, -135) * mm, "end": v(-15, -119.91) * mm});
            skLineSegment(sketch, "E90.MirrorCS", {"start": v(-14.93, -108) * mm, "end": v(-32.93, -90) * mm});
            skLineSegment(sketch, "E91.MirrorCS", {"start": v(0, -90) * mm, "end": v(0, -120) * mm, "construction": true});
            skLineSegment(sketch, "E92.MirrorCS", {"start": v(15, -108.9) * mm, "end": v(33.89, -90) * mm});
            skCircle(sketch, "E93.MirrorC", {"center": v(0, -120) * mm, "radius": 6 * mm});
            skSolve(sketch);
        }
        {
            var Q0;
            Q0=makeQuery(id+"F16.imprint","IMPRINT",FACE,{"disambiguationData":[TD([[makeQuery(id+"F16.imprint","IMPRINT",EDGE,{"derivedFrom":sQuery(id+"F16.wireOp",EDGE,"E80")}),-1.0]])]});
            var Q1;
            Q1=makeQuery(id+"F16.imprint","IMPRINT",FACE,{"disambiguationData":[TD([[makeQuery(id+"F16.imprint","IMPRINT",EDGE,{"derivedFrom":makeQuery(id+"F1.opExtrude","CAP_EDGE",EDGE,{"disambiguationData":[OSD([sQuery(id+"F0.wireOp",EDGE,"E1.left")])],"isStart":true})}),-1.0]])]});
            var Q2;
            Q2=makeQuery(id+"F16.imprint","IMPRINT",FACE,{"disambiguationData":[TD([[makeQuery(id+"F16.imprint","IMPRINT",EDGE,{"derivedFrom":sQuery(id+"F16.wireOp",EDGE,"E87.MirrorCS")}),-1.0]])]});
            var Q3;
            Q3=makeQuery(id+"F2.opExtrude","CAP_FACE",FACE,{"disambiguationData":[OSD([sQuery(id+"F0.wireOp",EDGE,"E12"),sQuery(id+"F0.wireOp",EDGE,"E13"),sQuery(id+"F0.wireOp",EDGE,"E14"),sQuery(id+"F0.wireOp",EDGE,"E15"),sQuery(id+"F0.wireOp",EDGE,"E17.filletArc"),sQuery(id+"F0.wireOp",EDGE,"E18.filletArc"),sQuery(id+"F0.wireOp",EDGE,"E19.filletArc"),sQuery(id+"F0.wireOp",EDGE,"E20.filletArc"),sQuery(id+"F0.wireOp",EDGE,"E25.0"),sQuery(id+"F0.wireOp",EDGE,"E25.1"),sQuery(id+"F0.wireOp",EDGE,"E25.2"),sQuery(id+"F0.wireOp",EDGE,"E25.3"),sQuery(id+"F0.wireOp",EDGE,"E25.4"),sQuery(id+"F0.wireOp",EDGE,"E25.5"),sQuery(id+"F0.wireOp",EDGE,"E25.6"),sQuery(id+"F0.wireOp",EDGE,"E25.7")])],"isStart":false});
            extrude(context, id + "F17", {"entities" : qUnion([Q0, Q1, Q2]), "operationType" : NewBodyOperationType.ADD, "endBound" : BoundingType.UP_TO_SURFACE, "endBoundEntityFace" : qUnion([Q3]), "depth" : 25 * mm});
        }
    });
